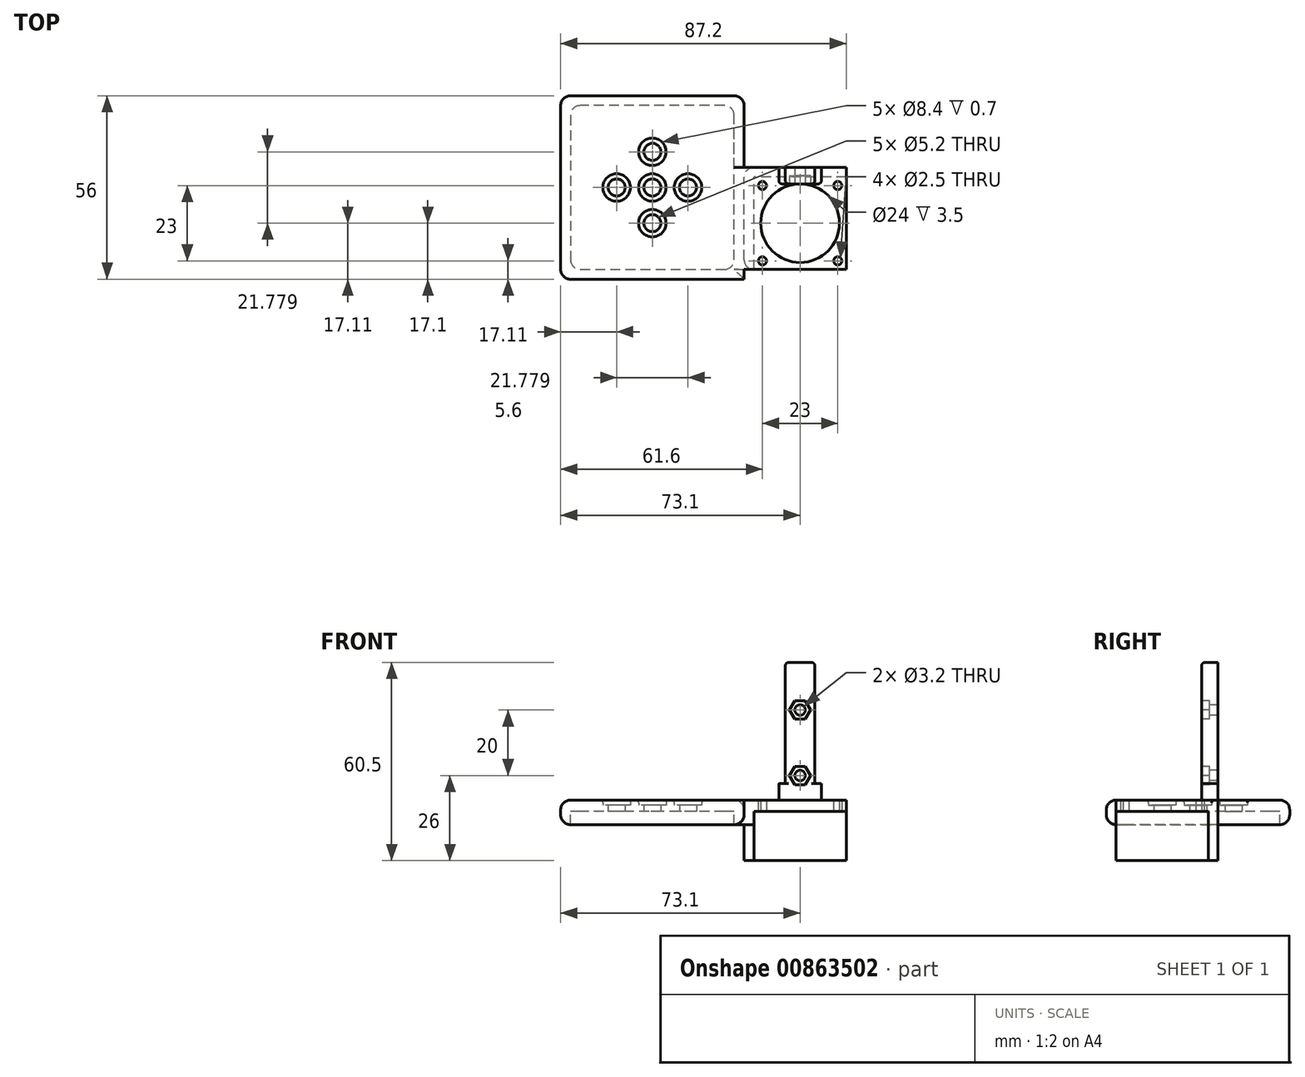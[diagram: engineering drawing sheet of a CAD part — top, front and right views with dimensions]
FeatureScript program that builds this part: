
annotation { "Feature Type Name" : "Feature", "Feature Type Description" : "" }
export const myFeature = defineFeature(function(context is Context, id is Id, definition is map)
    precondition{}
    {
        {
            var Q0;
            Q0=qCreatedBy(makeId("Top.planeOp"),FACE);
            var sketch = newSketch(context, id + "F0", { "sketchPlane" : qUnion([Q0])});
            skLineSegment(sketch, "E0.bottom", {"start": v(0, 0) * mm, "end": v(-28.2, 0) * mm});
            skLineSegment(sketch, "E0.top", {"start": v(0, 28.2) * mm, "end": v(-28.2, 28.2) * mm});
            skLineSegment(sketch, "E0.left", {"start": v(0, 0) * mm, "end": v(0, 28.2) * mm});
            skLineSegment(sketch, "E0.right", {"start": v(-28.2, 0) * mm, "end": v(-28.2, 28.2) * mm});
            skCircle(sketch, "E1", {"center": v(-14.1, 14.1) * mm, "radius": 12 * mm});
            skPoint(sketch, "E1.centerSnap0", {"position": v(0, 14.1) * mm});
            skPoint(sketch, "E1.centerSnap1", {"position": v(-14.1, 0) * mm});
            skCircle(sketch, "E2", {"center": v(-2.6, 25.6) * mm, "radius": 1.25 * mm});
            skCircle(sketch, "E3.0.1.0", {"center": v(-2.6, 2.6) * mm, "radius": 1.25 * mm});
            skCircle(sketch, "E3.1.0.0", {"center": v(-25.6, 25.6) * mm, "radius": 1.25 * mm});
            skCircle(sketch, "E3.1.1.0", {"center": v(-25.6, 2.6) * mm, "radius": 1.25 * mm});
            skLineSegment(sketch, "E3.direction1", {"start": v(-2.6, 25.6) * mm, "end": v(-25.6, 25.6) * mm, "construction": true});
            skLineSegment(sketch, "E3.direction2", {"start": v(-2.6, 25.6) * mm, "end": v(-2.6, 2.6) * mm, "construction": true});
            skPoint(sketch, "E4.startSnap0", {"position": v(-14.1, 25.6) * mm});
            skLineSegment(sketch, "E5", {"start": v(0, 31.1) * mm, "end": v(0, 28.2) * mm});
            skLineSegment(sketch, "E6", {"start": v(0, 31.1) * mm, "end": v(-28.2, 31.1) * mm});
            skLineSegment(sketch, "E7", {"start": v(-28.2, 31.1) * mm, "end": v(-28.2, 28.2) * mm});
            skLineSegment(sketch, "E8", {"start": v(-28.2, 0) * mm, "end": v(-31.2, 0) * mm});
            skLineSegment(sketch, "E9", {"start": v(-31.2, 0) * mm, "end": v(-31.2, -3) * mm, "construction": true});
            skLineSegment(sketch, "E10.bottom", {"start": v(-31.2, -3) * mm, "end": v(-87.2, -3) * mm});
            skLineSegment(sketch, "E10.top", {"start": v(-31.2, 53) * mm, "end": v(-87.2, 53) * mm});
            skLineSegment(sketch, "E10.left", {"start": v(-31.2, -3) * mm, "end": v(-31.2, 53) * mm});
            skLineSegment(sketch, "E10.right", {"start": v(-87.2, -3) * mm, "end": v(-87.2, 53) * mm});
            skLineSegment(sketch, "E11", {"start": v(-28.2, 31.1) * mm, "end": v(-31.2, 31.1) * mm});
            skLineSegment(sketch, "E12", {"start": v(-84.2, 50) * mm, "end": v(-84.2, 0) * mm});
            skLineSegment(sketch, "E13", {"start": v(-84.2, 0) * mm, "end": v(-34.2, 0) * mm});
            skLineSegment(sketch, "E14", {"start": v(-34.2, 0) * mm, "end": v(-34.2, 50) * mm});
            skLineSegment(sketch, "E15", {"start": v(-34.2, 50) * mm, "end": v(-84.2, 50) * mm});
            skPoint(sketch, "E16", {"position": v(-59.2, 25) * mm});
            skPoint(sketch, "E16.positionSnap0", {"position": v(-84.2, 25) * mm});
            skPoint(sketch, "E16.positionSnap1", {"position": v(-59.2, 50) * mm});
            skCircle(sketch, "E17", {"center": v(-59.2, 25) * mm, "radius": 2.6 * mm});
            skCircle(sketch, "E18", {"center": v(-59.2, 25) * mm, "radius": 4.2 * mm});
            skCircle(sketch, "E19", {"center": v(-59.2, 35.89) * mm, "radius": 2.6 * mm});
            skCircle(sketch, "E20", {"center": v(-59.2, 35.89) * mm, "radius": 4.2 * mm});
            skCircle(sketch, "E21.1.0", {"center": v(-70.09, 25) * mm, "radius": 2.6 * mm});
            skCircle(sketch, "E21.1.1", {"center": v(-70.09, 25) * mm, "radius": 4.2 * mm});
            skCircle(sketch, "E21.2.0", {"center": v(-59.2, 14.11) * mm, "radius": 2.6 * mm});
            skCircle(sketch, "E21.2.1", {"center": v(-59.2, 14.11) * mm, "radius": 4.2 * mm});
            skCircle(sketch, "E21.3.0", {"center": v(-48.31, 25) * mm, "radius": 2.6 * mm});
            skCircle(sketch, "E21.3.1", {"center": v(-48.31, 25) * mm, "radius": 4.2 * mm});
            skSolve(sketch);
        }
        {
            var Q0;
            {var subQ6=sQuery(id+"F0.wireOp",EDGE,"E0.bottom");Q0=makeQuery(id+"F0.imprint","IMPRINT",FACE,{"disambiguationData":[TD([[makeQuery(id+"F0.imprint","IMPRINT",EDGE,{"derivedFrom":subQ6}),-1.0]])]});}
            var Q1;
            {var subQ4=sQuery(id+"F0.wireOp",EDGE,"ijPHqbvI-z4L9-HcXl-GGPW-hylEVIwZFws3");Q1=makeQuery(id+"F0.imprint","IMPRINT",FACE,{"disambiguationData":[TD([[makeQuery(id+"F0.imprint","IMPRINT",EDGE,{"derivedFrom":subQ4}),-1.0]])]});}
            var Q2;
            {var subQ5=sQuery(id+"F0.wireOp",EDGE,"m2Cxr2Ga-0o2j-HVXw-7p58-Pcn7Cvv0tEOK");Q2=makeQuery(id+"F0.imprint","IMPRINT",FACE,{"disambiguationData":[TD([[makeQuery(id+"F0.imprint","IMPRINT",EDGE,{"derivedFrom":subQ5}),1.0]])]});}
            var Q3;
            Q3=makeQuery(id+"F0.imprint","IMPRINT",FACE,{"disambiguationData":[TD([[makeQuery(id+"F0.imprint","IMPRINT",EDGE,{"derivedFrom":sQuery(id+"F0.wireOp",EDGE,"8loH9SmV-sh9J-LUzo-QlBY-makiSQwsu6jr")}),-1.0]])]});
            var Q4;
            {var subQ0=sQuery(id+"F0.wireOp",EDGE,"9hWyS0dG-HEyQ-yypX-yeBZ-Q9COCQ3kwopz.top");Q4=makeQuery(id+"F0.imprint","IMPRINT",FACE,{"disambiguationData":[TD([[makeQuery(id+"F0.imprint","IMPRINT",EDGE,{"derivedFrom":subQ0}),-1.0]])]});}
            var Q5;
            {var subQ3=sQuery(id+"F0.wireOp",EDGE,"NLWkRKNC-S5Q5-cDU1-KmpY-qmc1vbDf303U");Q5=makeQuery(id+"F0.imprint","IMPRINT",FACE,{"disambiguationData":[TD([[makeQuery(id+"F0.imprint","IMPRINT",EDGE,{"derivedFrom":subQ3}),1.0]])]});}
            var Q6;
            {var subQ0=sQuery(id+"F0.wireOp",EDGE,"9hWyS0dG-HEyQ-yypX-yeBZ-Q9COCQ3kwopz.bottom");Q6=makeQuery(id+"F0.imprint","IMPRINT",FACE,{"disambiguationData":[TD([[makeQuery(id+"F0.imprint","IMPRINT",EDGE,{"derivedFrom":subQ0}),1.0]])]});}
            var Q7;
            {var subQ6=sQuery(id+"F0.wireOp",EDGE,"E4");Q7=makeQuery(id+"F0.imprint","IMPRINT",FACE,{"disambiguationData":[TD([[makeQuery(id+"F0.imprint","IMPRINT",EDGE,{"derivedFrom":subQ6}),-1.0]])]});}
            var Q8;
            {var subQ5=sQuery(id+"F0.wireOp",EDGE,"mFEbcyhE-I2m0-IbpG-fMGd-iVe9TuxLjYg8");Q8=makeQuery(id+"F0.imprint","IMPRINT",FACE,{"disambiguationData":[TD([[makeQuery(id+"F0.imprint","IMPRINT",EDGE,{"derivedFrom":subQ5}),-1.0]])]});}
            var Q9;
            {var subQ0=sQuery(id+"F0.wireOp",EDGE,"E0.top");Q9=makeQuery(id+"F0.imprint","IMPRINT",FACE,{"disambiguationData":[TD([[makeQuery(id+"F0.imprint","IMPRINT",EDGE,{"derivedFrom":subQ0}),-1.0]])]});}
            var Q10;
            {var subQ5=sQuery(id+"F0.wireOp",EDGE,"lu1baBKB-0tmX-wPb9-EPOR-MeIyYVtMshRU");Q10=makeQuery(id+"F0.imprint","IMPRINT",FACE,{"disambiguationData":[TD([[makeQuery(id+"F0.imprint","IMPRINT",EDGE,{"derivedFrom":subQ5}),-1.0]])]});}
            var Q11;
            {var subQ1=sQuery(id+"F0.wireOp",EDGE,"7PjgIpir-cJoU-ZLOv-uaDD-36FM32oQSfDl.top");Q11=makeQuery(id+"F0.imprint","IMPRINT",FACE,{"disambiguationData":[TD([[makeQuery(id+"F0.imprint","IMPRINT",EDGE,{"derivedFrom":subQ1}),1.0]])]});}
            var Q12;
            {var subQ3=sQuery(id+"F0.wireOp",EDGE,"xbB81sAq-Xaiy-Ms8t-QkRO-Xj2NnZmD8rnq");Q12=makeQuery(id+"F0.imprint","IMPRINT",FACE,{"disambiguationData":[TD([[makeQuery(id+"F0.imprint","IMPRINT",EDGE,{"derivedFrom":subQ3}),-1.0]])]});}
            var Q13;
            Q13=makeQuery(id+"F0.imprint","IMPRINT",FACE,{"disambiguationData":[TD([[makeQuery(id+"F0.imprint","IMPRINT",EDGE,{"derivedFrom":sQuery(id+"F0.wireOp",EDGE,"E0.right")}),1.0]])]});
            var Q14;
            {var subQ0=sQuery(id+"F0.wireOp",EDGE,"XYQOdFon-8ze7-kMVV-HPu9-pt2qhsvfgXNz");Q14=makeQuery(id+"F0.imprint","IMPRINT",FACE,{"disambiguationData":[TD([[makeQuery(id+"F0.imprint","IMPRINT",EDGE,{"derivedFrom":subQ0}),1.0]])]});}
            var Q15;
            {var subQ3=sQuery(id+"F0.wireOp",EDGE,"bGz3AujC-m2g5-EDBu-aNqw-dt0JoBSHWJhe");Q15=makeQuery(id+"F0.imprint","IMPRINT",FACE,{"disambiguationData":[TD([[makeQuery(id+"F0.imprint","IMPRINT",EDGE,{"derivedFrom":subQ3}),-1.0]])]});}
            var Q16;
            {var subQ0=sQuery(id+"F0.wireOp",EDGE,"qGMF6F5y-CSdx-2Ybo-XQKX-Ya8MyXLlpcJf");Q16=makeQuery(id+"F0.imprint","IMPRINT",FACE,{"disambiguationData":[TD([[makeQuery(id+"F0.imprint","IMPRINT",EDGE,{"derivedFrom":subQ0}),-1.0]])]});}
            var Q17;
            {var subQ4=sQuery(id+"F0.wireOp",EDGE,"E10.bottom");Q17=makeQuery(id+"F0.imprint","IMPRINT",FACE,{"disambiguationData":[TD([[makeQuery(id+"F0.imprint","IMPRINT",EDGE,{"derivedFrom":subQ4}),-1.0]])]});}
            var Q18;
            {var subQ0=sQuery(id+"F0.wireOp",EDGE,"PibB2iq3-5r3C-sdaA-aypm-pyxTfNWSrPnX");Q18=makeQuery(id+"F0.imprint","IMPRINT",FACE,{"disambiguationData":[TD([[makeQuery(id+"F0.imprint","IMPRINT",EDGE,{"derivedFrom":subQ0}),1.0]])]});}
            var Q19;
            Q19=makeQuery(id+"F0.imprint","IMPRINT",FACE,{"disambiguationData":[TD([[makeQuery(id+"F0.imprint","IMPRINT",EDGE,{"derivedFrom":sQuery(id+"F0.wireOp",EDGE,"E12")}),1.0]])]});
            extrude(context, id + "F1", {"entities" : qUnion([Q0, Q1, Q2, Q3, Q4, Q5, Q6, Q7, Q8, Q9, Q10, Q11, Q12, Q13, Q14, Q15, Q16, Q17, Q18, Q19]), "depth" : 3.5 * mm, "offsetDistance" : 25 * mm});
        }
        {
            var Q0;
            {var subQ4=sQuery(id+"F0.wireOp",EDGE,"E10.bottom");Q0=makeQuery(id+"F0.imprint","IMPRINT",FACE,{"disambiguationData":[TD([[makeQuery(id+"F0.imprint","IMPRINT",EDGE,{"derivedFrom":subQ4}),-1.0]])]});}
            extrude(context, id + "F2", {"entities" : qUnion([Q0]), "operationType" : NewBodyOperationType.ADD, "oppositeDirection" : true, "depth" : 4 * mm, "offsetDistance" : 25 * mm});
        }
        {
            var Q0;
            Q0=makeQuery(id+"F0.imprint","IMPRINT",FACE,{"disambiguationData":[TD([[makeQuery(id+"F0.imprint","IMPRINT",EDGE,{"derivedFrom":sQuery(id+"F0.wireOp",EDGE,"E19")}),-1.0]])]});
            var Q1;
            Q1=makeQuery(id+"F0.imprint","IMPRINT",FACE,{"disambiguationData":[TD([[makeQuery(id+"F0.imprint","IMPRINT",EDGE,{"derivedFrom":sQuery(id+"F0.wireOp",EDGE,"E21.3.0")}),-1.0]])]});
            var Q2;
            Q2=makeQuery(id+"F0.imprint","IMPRINT",FACE,{"disambiguationData":[TD([[makeQuery(id+"F0.imprint","IMPRINT",EDGE,{"derivedFrom":sQuery(id+"F0.wireOp",EDGE,"E17")}),-1.0]])]});
            var Q3;
            Q3=makeQuery(id+"F0.imprint","IMPRINT",FACE,{"disambiguationData":[TD([[makeQuery(id+"F0.imprint","IMPRINT",EDGE,{"derivedFrom":sQuery(id+"F0.wireOp",EDGE,"E21.1.0")}),-1.0]])]});
            var Q4;
            Q4=makeQuery(id+"F0.imprint","IMPRINT",FACE,{"disambiguationData":[TD([[makeQuery(id+"F0.imprint","IMPRINT",EDGE,{"derivedFrom":sQuery(id+"F0.wireOp",EDGE,"E21.2.0")}),-1.0]])]});
            extrude(context, id + "F3", {"entities" : qUnion([Q0, Q1, Q2, Q3, Q4]), "operationType" : NewBodyOperationType.ADD, "depth" : 2 * mm, "offsetDistance" : 25 * mm});
        }
        {
            var Q0;
            Q0=makeQuery(id+"F1.opExtrude","CAP_FACE",FACE,{"disambiguationData":[OSD([sQuery(id+"F0.wireOp",EDGE,"E0.bottom"),sQuery(id+"F0.wireOp",EDGE,"E0.left"),sQuery(id+"F0.wireOp",EDGE,"E1"),sQuery(id+"F0.wireOp",EDGE,"E2"),sQuery(id+"F0.wireOp",EDGE,"E3.0.1.0"),sQuery(id+"F0.wireOp",EDGE,"E3.1.0.0"),sQuery(id+"F0.wireOp",EDGE,"E3.1.1.0"),sQuery(id+"F0.wireOp",EDGE,"9hWyS0dG-HEyQ-yypX-yeBZ-Q9COCQ3kwopz.bottom"),sQuery(id+"F0.wireOp",EDGE,"9hWyS0dG-HEyQ-yypX-yeBZ-Q9COCQ3kwopz.top"),sQuery(id+"F0.wireOp",EDGE,"9hWyS0dG-HEyQ-yypX-yeBZ-Q9COCQ3kwopz.left"),sQuery(id+"F0.wireOp",EDGE,"8loH9SmV-sh9J-LUzo-QlBY-makiSQwsu6jr"),sQuery(id+"F0.wireOp",EDGE,"cz2AWorx-eusL-XrBm-fWZu-7YGwTg6LLj23"),sQuery(id+"F0.wireOp",EDGE,"029e4b47-2b3b-455f-a0ee-34a0f4a43a5b.1.1"),sQuery(id+"F0.wireOp",EDGE,"029e4b47-2b3b-455f-a0ee-34a0f4a43a5b.2.1"),sQuery(id+"F0.wireOp",EDGE,"029e4b47-2b3b-455f-a0ee-34a0f4a43a5b.3.1"),sQuery(id+"F0.wireOp",EDGE,"NLWkRKNC-S5Q5-cDU1-KmpY-qmc1vbDf303U"),sQuery(id+"F0.wireOp",EDGE,"zs0ojhJG-X6Sq-BrWQ-kWkG-rbSZWmPVnEDv"),sQuery(id+"F0.wireOp",EDGE,"vGF2y9MP-X188-q6Oo-Al50-q7mYZCjIZBZr"),sQuery(id+"F0.wireOp",EDGE,"E5"),sQuery(id+"F0.wireOp",EDGE,"E6")])],"isStart":false});
            var sketch = newSketch(context, id + "F4", { "sketchPlane" : qUnion([Q0])});
            skLineSegment(sketch, "E22", {"start": v(-14.1, 26.1) * mm, "end": v(-18.6, 26.1) * mm});
            skLineSegment(sketch, "E23", {"start": v(-18.6, 26.1) * mm, "end": v(-18.6, 31.1) * mm});
            skLineSegment(sketch, "E24", {"start": v(-18.6, 31.1) * mm, "end": v(-9.6, 31.1) * mm});
            skLineSegment(sketch, "E25", {"start": v(-9.6, 31.1) * mm, "end": v(-9.6, 26.1) * mm});
            skLineSegment(sketch, "E26", {"start": v(-9.6, 26.1) * mm, "end": v(-14.1, 26.1) * mm});
            skLineSegment(sketch, "E27", {"start": v(-18.6, 26.1) * mm, "end": v(-20.6, 26.1) * mm});
            skLineSegment(sketch, "E28", {"start": v(-20.6, 26.1) * mm, "end": v(-20.6, 31.1) * mm});
            skLineSegment(sketch, "E29", {"start": v(-20.6, 31.1) * mm, "end": v(-18.6, 31.1) * mm});
            skLineSegment(sketch, "E30", {"start": v(-9.6, 26.1) * mm, "end": v(-7.6, 26.1) * mm});
            skLineSegment(sketch, "E31", {"start": v(-7.6, 26.1) * mm, "end": v(-7.6, 31.1) * mm});
            skLineSegment(sketch, "E32", {"start": v(-7.6, 31.1) * mm, "end": v(-9.6, 31.1) * mm});
            skSolve(sketch);
        }
        {
            var Q0;
            Q0=makeQuery(id+"F4.imprint","IMPRINT",FACE,{"disambiguationData":[TD([[makeQuery(id+"F4.imprint","IMPRINT",EDGE,{"derivedFrom":sQuery(id+"F4.wireOp",EDGE,"E22")}),-1.0]])]});
            extrude(context, id + "F5", {"entities" : qUnion([Q0]), "operationType" : NewBodyOperationType.ADD, "depth" : 42 * mm, "offsetDistance" : 25 * mm});
        }
        {
            var Q0;
            Q0=makeQuery(id+"F4.imprint","IMPRINT",FACE,{"disambiguationData":[TD([[makeQuery(id+"F4.imprint","IMPRINT",EDGE,{"derivedFrom":sQuery(id+"F4.wireOp",EDGE,"E23")}),1.0]])]});
            var Q1;
            Q1=makeQuery(id+"F4.imprint","IMPRINT",FACE,{"disambiguationData":[TD([[makeQuery(id+"F4.imprint","IMPRINT",EDGE,{"derivedFrom":sQuery(id+"F4.wireOp",EDGE,"E25")}),1.0]])]});
            extrude(context, id + "F6", {"entities" : qUnion([Q0, Q1]), "operationType" : NewBodyOperationType.ADD, "depth" : 5 * mm, "offsetDistance" : 25 * mm});
        }
        {
            var Q0;
            Q0=makeQuery(id+"F5.opExtrude","SWEPT_FACE",FACE,{"disambiguationData":[OSD([sQuery(id+"F4.wireOp",EDGE,"E22"),sQuery(id+"F4.wireOp",EDGE,"E26")])]});
            var sketch = newSketch(context, id + "F7", { "sketchPlane" : qUnion([Q0])});
            skLineSegment(sketch, "E33", {"start": v(-14.1, 45.5) * mm, "end": v(-14.1, 3.5) * mm, "construction": true});
            skCircle(sketch, "E34", {"center": v(-14.1, 11) * mm, "radius": 1.6 * mm});
            skCircle(sketch, "E35", {"center": v(-14.1, 31) * mm, "radius": 1.6 * mm});
            skCircle(sketch, "E36.cCircle", {"center": v(-14.1, 11) * mm, "radius": 2.8 * mm, "construction": true});
            skLineSegment(sketch, "E36.0", {"start": v(-15.72, 13.8) * mm, "end": v(-12.48, 13.8) * mm});
            skLineSegment(sketch, "E36.1", {"start": v(-12.48, 13.8) * mm, "end": v(-10.87, 11) * mm});
            skLineSegment(sketch, "E36.2", {"start": v(-10.87, 11) * mm, "end": v(-12.48, 8.2) * mm});
            skLineSegment(sketch, "E36.3", {"start": v(-12.48, 8.2) * mm, "end": v(-15.72, 8.2) * mm});
            skLineSegment(sketch, "E36.4", {"start": v(-15.72, 8.2) * mm, "end": v(-17.33, 11) * mm});
            skLineSegment(sketch, "E36.5", {"start": v(-17.33, 11) * mm, "end": v(-15.72, 13.8) * mm});
            skPoint(sketch, "E36.0.midPoint", {"position": v(-14.1, 13.8) * mm});
            skCircle(sketch, "E37.cCircle", {"center": v(-14.1, 31) * mm, "radius": 2.8 * mm, "construction": true});
            skLineSegment(sketch, "E37.0", {"start": v(-15.72, 33.8) * mm, "end": v(-12.48, 33.8) * mm});
            skLineSegment(sketch, "E37.1", {"start": v(-12.48, 33.8) * mm, "end": v(-10.87, 31) * mm});
            skLineSegment(sketch, "E37.2", {"start": v(-10.87, 31) * mm, "end": v(-12.48, 28.2) * mm});
            skLineSegment(sketch, "E37.3", {"start": v(-12.48, 28.2) * mm, "end": v(-15.72, 28.2) * mm});
            skLineSegment(sketch, "E37.4", {"start": v(-15.72, 28.2) * mm, "end": v(-17.33, 31) * mm});
            skLineSegment(sketch, "E37.5", {"start": v(-17.33, 31) * mm, "end": v(-15.72, 33.8) * mm});
            skPoint(sketch, "E37.0.midPoint", {"position": v(-14.1, 33.8) * mm});
            skSolve(sketch);
        }
        {
            var Q0;
            Q0=makeQuery(id+"F7.imprint","IMPRINT",FACE,{"disambiguationData":[TD([[makeQuery(id+"F7.imprint","IMPRINT",EDGE,{"derivedFrom":sQuery(id+"F7.wireOp",EDGE,"E35")}),1.0]])]});
            var Q1;
            Q1=makeQuery(id+"F7.imprint","IMPRINT",FACE,{"disambiguationData":[TD([[makeQuery(id+"F7.imprint","IMPRINT",EDGE,{"derivedFrom":sQuery(id+"F7.wireOp",EDGE,"E34")}),1.0]])]});
            extrude(context, id + "F8", {"entities" : qUnion([Q0, Q1]), "operationType" : NewBodyOperationType.REMOVE, "oppositeDirection" : true, "depth" : 6 * mm, "offsetDistance" : 25 * mm});
        }
        {
            var Q0;
            Q0=makeQuery(id+"F7.imprint","IMPRINT",FACE,{"disambiguationData":[TD([[makeQuery(id+"F7.imprint","IMPRINT",EDGE,{"derivedFrom":sQuery(id+"F7.wireOp",EDGE,"E35")}),-1.0]])]});
            var Q1;
            Q1=makeQuery(id+"F7.imprint","IMPRINT",FACE,{"disambiguationData":[TD([[makeQuery(id+"F7.imprint","IMPRINT",EDGE,{"derivedFrom":sQuery(id+"F7.wireOp",EDGE,"E34")}),-1.0]])]});
            extrude(context, id + "F9", {"entities" : qUnion([Q0, Q1]), "operationType" : NewBodyOperationType.REMOVE, "oppositeDirection" : true, "depth" : 2.5 * mm, "offsetDistance" : 25 * mm});
        }
        {
            var Q0;
            Q0=makeQuery(id+"F0.imprint","IMPRINT",FACE,{"disambiguationData":[TD([[makeQuery(id+"F0.imprint","IMPRINT",EDGE,{"derivedFrom":sQuery(id+"F0.wireOp",EDGE,"E0.right")}),1.0]])]});
            extrude(context, id + "F10", {"entities" : qUnion([Q0]), "operationType" : NewBodyOperationType.ADD, "oppositeDirection" : true, "depth" : 15 * mm, "offsetDistance" : 25 * mm});
        }
        {
            var Q0;
            Q0=makeQuery(id+"F5.opExtrude","SWEPT_EDGE",EDGE,{"disambiguationData":[OSD([sQuery(id+"F4.wireOp",EDGE,"E22"),sQuery(id+"F4.wireOp",EDGE,"E23")])]});
            var Q1;
            Q1=makeQuery(id+"F5.opExtrude","SWEPT_EDGE",EDGE,{"disambiguationData":[OSD([sQuery(id+"F4.wireOp",EDGE,"E25"),sQuery(id+"F4.wireOp",EDGE,"E26")])]});
            var Q2;
            Q2=makeQuery(id+"F5.opExtrude","CAP_EDGE",EDGE,{"disambiguationData":[OSD([sQuery(id+"F4.wireOp",EDGE,"E22"),sQuery(id+"F4.wireOp",EDGE,"E26")])],"isStart":false});
            var Q3;
            Q3=makeQuery(id+"F5.opExtrude","CAP_EDGE",EDGE,{"disambiguationData":[OSD([sQuery(id+"F4.wireOp",EDGE,"E25")])],"isStart":false});
            var Q4;
            Q4=makeQuery(id+"F5.opExtrude","CAP_EDGE",EDGE,{"disambiguationData":[OSD([sQuery(id+"F4.wireOp",EDGE,"E23")])],"isStart":false});
            var Q5;
            Q5=makeQuery(id+"F6.opExtrude","SWEPT_EDGE",EDGE,{"disambiguationData":[OSD([sQuery(id+"F4.wireOp",EDGE,"E27"),sQuery(id+"F4.wireOp",EDGE,"E28")])]});
            var Q6;
            Q6=makeQuery(id+"F6.opExtrude","SWEPT_EDGE",EDGE,{"disambiguationData":[OSD([sQuery(id+"F4.wireOp",EDGE,"E30"),sQuery(id+"F4.wireOp",EDGE,"E31")])]});
            var Q7;
            Q7=makeQuery(id+"F6.opExtrude","CAP_EDGE",EDGE,{"disambiguationData":[OSD([sQuery(id+"F4.wireOp",EDGE,"E31")])],"isStart":true});
            fillet(context, id + "F11", {"entities" : qUnion([Q0, Q1, Q2, Q3, Q4, Q5, Q6, Q7]), "tangentPropagation" : true, "radius" : 1 * mm, "defaultsChanged" : false, "vertexSettings" : [], "allowEdgeOverflow" : false});
        }
        {
            var Q0;
            Q0=makeQuery(id+"F1.opExtrude","CAP_EDGE",EDGE,{"disambiguationData":[OSD([sQuery(id+"F0.wireOp",EDGE,"E20")])],"isStart":false});
            var Q1;
            Q1=makeQuery(id+"F1.opExtrude","CAP_EDGE",EDGE,{"disambiguationData":[OSD([sQuery(id+"F0.wireOp",EDGE,"E21.3.1")])],"isStart":false});
            var Q2;
            Q2=makeQuery(id+"F1.opExtrude","CAP_EDGE",EDGE,{"disambiguationData":[OSD([sQuery(id+"F0.wireOp",EDGE,"E18")])],"isStart":false});
            var Q3;
            Q3=makeQuery(id+"F1.opExtrude","CAP_EDGE",EDGE,{"disambiguationData":[OSD([sQuery(id+"F0.wireOp",EDGE,"E21.1.1")])],"isStart":false});
            var Q4;
            Q4=makeQuery(id+"F1.opExtrude","CAP_EDGE",EDGE,{"disambiguationData":[OSD([sQuery(id+"F0.wireOp",EDGE,"E21.2.1")])],"isStart":false});
            fillet(context, id + "F12", {"entities" : qUnion([Q0, Q1, Q2, Q3, Q4]), "tangentPropagation" : true, "radius" : 0.8 * mm, "defaultsChanged" : false, "vertexSettings" : [], "allowEdgeOverflow" : false});
        }
        {
            var Q0;
            {var subQ0=sQuery(id+"F0.wireOp",EDGE,"E10.right");var subQ1=sQuery(id+"F0.wireOp",EDGE,"E10.bottom");Q0=makeQuery(id+"F2.boolean.opBoolean","MERGE",EDGE,{"derivedFrom":[makeQuery(id+"F1.opExtrude","SWEPT_EDGE",EDGE,{"disambiguationData":[OSD([subQ1,subQ0])]}),makeQuery(id+"F2.opExtrude","SWEPT_EDGE",EDGE,{"disambiguationData":[OSD([subQ1,subQ0])]})]});}
            var Q1;
            Q1=makeQuery(id+"F2.opExtrude","SWEPT_EDGE",EDGE,{"disambiguationData":[OSD([sQuery(id+"F0.wireOp",EDGE,"E12"),sQuery(id+"F0.wireOp",EDGE,"E13")])]});
            var Q2;
            Q2=makeQuery(id+"F2.opExtrude","SWEPT_EDGE",EDGE,{"disambiguationData":[OSD([sQuery(id+"F0.wireOp",EDGE,"E13"),sQuery(id+"F0.wireOp",EDGE,"E14")])]});
            var Q3;
            Q3=makeQuery(id+"F2.opExtrude","SWEPT_EDGE",EDGE,{"disambiguationData":[OSD([sQuery(id+"F0.wireOp",EDGE,"E14"),sQuery(id+"F0.wireOp",EDGE,"E15")])]});
            var Q4;
            Q4=makeQuery(id+"F2.opExtrude","SWEPT_EDGE",EDGE,{"disambiguationData":[OSD([sQuery(id+"F0.wireOp",EDGE,"E12"),sQuery(id+"F0.wireOp",EDGE,"E15")])]});
            var Q5;
            {var subQ0=sQuery(id+"F0.wireOp",EDGE,"E10.right");var subQ1=sQuery(id+"F0.wireOp",EDGE,"E10.top");Q5=makeQuery(id+"F2.boolean.opBoolean","MERGE",EDGE,{"derivedFrom":[makeQuery(id+"F1.opExtrude","SWEPT_EDGE",EDGE,{"disambiguationData":[OSD([subQ1,subQ0])]}),makeQuery(id+"F2.opExtrude","SWEPT_EDGE",EDGE,{"disambiguationData":[OSD([subQ1,subQ0])]})]});}
            var Q6;
            {var subQ0=sQuery(id+"F0.wireOp",EDGE,"E10.left");var subQ1=sQuery(id+"F0.wireOp",EDGE,"E10.top");Q6=makeQuery(id+"F2.boolean.opBoolean","MERGE",EDGE,{"derivedFrom":[makeQuery(id+"F1.opExtrude","SWEPT_EDGE",EDGE,{"disambiguationData":[OSD([subQ1,subQ0])]}),makeQuery(id+"F2.opExtrude","SWEPT_EDGE",EDGE,{"disambiguationData":[OSD([subQ1,subQ0])]})]});}
            var Q7;
            Q7=makeQuery(id+"F1.opExtrude","CAP_EDGE",EDGE,{"disambiguationData":[OSD([sQuery(id+"F0.wireOp",EDGE,"E10.right")])],"isStart":false});
            var Q8;
            Q8=makeQuery(id+"F1.opExtrude","CAP_EDGE",EDGE,{"disambiguationData":[OSD([sQuery(id+"F0.wireOp",EDGE,"E10.top")])],"isStart":false});
            var Q9;
            {var subQ0=sQuery(id+"F0.wireOp",EDGE,"E10.left");Q9=makeQuery(id+"F1.opExtrude","CAP_EDGE",EDGE,{"disambiguationData":[OSD([subQ0]),TDD([makeQuery(id+"F0.imprint","IMPRINT",EDGE,{"disambiguationData":[TD([[makeQuery(id+"F0.imprint","INTERSECT",VERTEX,{"derivedFrom":[sQuery(id+"F0.wireOp",EDGE,"E10.top"),subQ0]}),1.0]])],"derivedFrom":subQ0})])],"isStart":false});}
            var Q10;
            Q10=makeQuery(id+"F1.opExtrude","CAP_EDGE",EDGE,{"disambiguationData":[OSD([sQuery(id+"F0.wireOp",EDGE,"E10.bottom")])],"isStart":false});
            fillet(context, id + "F13", {"entities" : qUnion([Q0, Q1, Q2, Q3, Q4, Q5, Q6, Q7, Q8, Q9, Q10]), "tangentPropagation" : true, "radius" : 3 * mm, "defaultsChanged" : true, "vertexSettings" : [], "allowEdgeOverflow" : false});
        }
        {
            var Q0;
            {var subQ0=sQuery(id+"F0.wireOp",EDGE,"E10.left");Q0=makeQuery(id+"F10.boolean.opBoolean","SPLIT",EDGE,{"disambiguationData":[topologyDisambiguationEdgeConnected([makeQuery(id+"F2.opExtrude","CAP_FACE",FACE,{"disambiguationData":[OSD([sQuery(id+"F0.wireOp",EDGE,"E10.bottom"),sQuery(id+"F0.wireOp",EDGE,"E10.top"),subQ0,sQuery(id+"F0.wireOp",EDGE,"E10.right"),sQuery(id+"F0.wireOp",EDGE,"E12"),sQuery(id+"F0.wireOp",EDGE,"E13"),sQuery(id+"F0.wireOp",EDGE,"E14"),sQuery(id+"F0.wireOp",EDGE,"E15")])],"isStart":false}),makeQuery(id+"F10.opExtrude","SWEPT_FACE",FACE,{"disambiguationData":[OSD([subQ0])]})])],"derivedFrom":makeQuery(id+"F2.opExtrude","CAP_EDGE",EDGE,{"disambiguationData":[OSD([subQ0])],"isStart":false})});}
            fillet(context, id + "F14", {"entities" : qUnion([Q0]), "tangentPropagation" : true, "radius" : 3 * mm, "defaultsChanged" : false, "vertexSettings" : [], "allowEdgeOverflow" : false});
        }
        {
            var Q0;
            {var subQ0=sQuery(id+"F0.wireOp",EDGE,"E11");var subQ1=sQuery(id+"F0.wireOp",EDGE,"E10.left");var subQ2=sQuery(id+"F0.wireOp",EDGE,"E10.bottom");var subQ3=sQuery(id+"F0.wireOp",EDGE,"E10.top");Q0=makeQuery(id+"F14.opFillet","TWEAK_EDGE",EDGE,{"derivedFrom":[makeQuery(id+"F10.boolean.opBoolean","TWEAK_VERTEX",VERTEX,{"derivedFrom":[makeQuery(id+"F2.opExtrude","CAP_FACE",FACE,{"disambiguationData":[OSD([subQ2,subQ3,subQ1,sQuery(id+"F0.wireOp",EDGE,"E10.right"),sQuery(id+"F0.wireOp",EDGE,"E12"),sQuery(id+"F0.wireOp",EDGE,"E13"),sQuery(id+"F0.wireOp",EDGE,"E14"),sQuery(id+"F0.wireOp",EDGE,"E15")])],"isStart":false}),makeQuery(id+"F2.boolean.opBoolean","MERGE",FACE,{"derivedFrom":[makeQuery(id+"F1.opExtrude","SWEPT_FACE",FACE,{"disambiguationData":[OSD([subQ1]),TDD([makeQuery(id+"F0.imprint","IMPRINT",EDGE,{"disambiguationData":[TD([[makeQuery(id+"F0.imprint","INTERSECT",VERTEX,{"derivedFrom":[subQ3,subQ1]}),1.0]])],"derivedFrom":subQ1})])]}),makeQuery(id+"F1.opExtrude","SWEPT_FACE",FACE,{"disambiguationData":[OSD([subQ1]),TDD([makeQuery(id+"F0.imprint","IMPRINT",EDGE,{"disambiguationData":[TD([[makeQuery(id+"F0.imprint","INTERSECT",VERTEX,{"derivedFrom":[sQuery(id+"F0.wireOp",EDGE,"E8"),subQ1]}),1.0]])],"derivedFrom":subQ1})])]}),makeQuery(id+"F2.opExtrude","SWEPT_FACE",FACE,{"disambiguationData":[OSD([subQ1])]})]}),makeQuery(id+"F5.boolean.opBoolean","MERGE",FACE,{"derivedFrom":[makeQuery(id+"F1.opExtrude","SWEPT_FACE",FACE,{"disambiguationData":[OSD([sQuery(id+"F0.wireOp",EDGE,"E6"),subQ0])]}),makeQuery(id+"F5.opExtrude","SWEPT_FACE",FACE,{"disambiguationData":[OSD([sQuery(id+"F4.wireOp",EDGE,"E24")])]})]}),makeQuery(id+"F10.opExtrude","SWEPT_FACE",FACE,{"disambiguationData":[OSD([subQ1])]}),makeQuery(id+"F10.opExtrude","SWEPT_FACE",FACE,{"disambiguationData":[OSD([subQ0])]})]})]});}
            var Q1;
            {var subQ0=sQuery(id+"F0.wireOp",EDGE,"E11");var subQ1=sQuery(id+"F0.wireOp",EDGE,"E10.left");Q1=makeQuery(id+"F10.boolean.opBoolean","MERGE",EDGE,{"derivedFrom":[makeQuery(id+"F1.opExtrude","SWEPT_EDGE",EDGE,{"disambiguationData":[OSD([subQ1,subQ0])]}),makeQuery(id+"F10.opExtrude","SWEPT_EDGE",EDGE,{"disambiguationData":[OSD([subQ1,subQ0])]})]});}
            var Q2;
            {var subQ0=sQuery(id+"F0.wireOp",EDGE,"E10.left");var subQ1=sQuery(id+"F0.wireOp",EDGE,"E8");Q2=makeQuery(id+"F10.boolean.opBoolean","MERGE",EDGE,{"derivedFrom":[makeQuery(id+"F1.opExtrude","SWEPT_EDGE",EDGE,{"disambiguationData":[OSD([subQ1,subQ0])]}),makeQuery(id+"F10.opExtrude","SWEPT_EDGE",EDGE,{"disambiguationData":[OSD([subQ1,subQ0])]})]});}
            var Q3;
            {var subQ0=sQuery(id+"F0.wireOp",EDGE,"E10.left");var subQ1=sQuery(id+"F0.wireOp",EDGE,"E8");var subQ2=sQuery(id+"F0.wireOp",EDGE,"E10.bottom");var subQ3=sQuery(id+"F0.wireOp",EDGE,"E10.top");Q3=makeQuery(id+"F14.opFillet","TWEAK_EDGE",EDGE,{"derivedFrom":[makeQuery(id+"F10.boolean.opBoolean","TWEAK_VERTEX",VERTEX,{"derivedFrom":[makeQuery(id+"F1.opExtrude","SWEPT_FACE",FACE,{"disambiguationData":[OSD([sQuery(id+"F0.wireOp",EDGE,"E0.bottom"),subQ1])]}),makeQuery(id+"F2.opExtrude","CAP_FACE",FACE,{"disambiguationData":[OSD([subQ2,subQ3,subQ0,sQuery(id+"F0.wireOp",EDGE,"E10.right"),sQuery(id+"F0.wireOp",EDGE,"E12"),sQuery(id+"F0.wireOp",EDGE,"E13"),sQuery(id+"F0.wireOp",EDGE,"E14"),sQuery(id+"F0.wireOp",EDGE,"E15")])],"isStart":false}),makeQuery(id+"F2.boolean.opBoolean","MERGE",FACE,{"derivedFrom":[makeQuery(id+"F1.opExtrude","SWEPT_FACE",FACE,{"disambiguationData":[OSD([subQ0]),TDD([makeQuery(id+"F0.imprint","IMPRINT",EDGE,{"disambiguationData":[TD([[makeQuery(id+"F0.imprint","INTERSECT",VERTEX,{"derivedFrom":[subQ3,subQ0]}),1.0]])],"derivedFrom":subQ0})])]}),makeQuery(id+"F1.opExtrude","SWEPT_FACE",FACE,{"disambiguationData":[OSD([subQ0]),TDD([makeQuery(id+"F0.imprint","IMPRINT",EDGE,{"disambiguationData":[TD([[makeQuery(id+"F0.imprint","INTERSECT",VERTEX,{"derivedFrom":[subQ1,subQ0]}),1.0]])],"derivedFrom":subQ0})])]}),makeQuery(id+"F2.opExtrude","SWEPT_FACE",FACE,{"disambiguationData":[OSD([subQ0])]})]}),makeQuery(id+"F10.opExtrude","SWEPT_FACE",FACE,{"disambiguationData":[OSD([subQ1])]}),makeQuery(id+"F10.opExtrude","SWEPT_FACE",FACE,{"disambiguationData":[OSD([subQ0])]})]})]});}
            fillet(context, id + "F15", {"entities" : qUnion([Q0, Q1, Q2, Q3]), "tangentPropagation" : true, "radius" : 3 * mm, "defaultsChanged" : false, "vertexSettings" : [], "allowEdgeOverflow" : false});
        }
        {
            var Q0;
            Q0=makeQuery(id+"F0.imprint","IMPRINT",FACE,{"disambiguationData":[TD([[makeQuery(id+"F0.imprint","IMPRINT",EDGE,{"derivedFrom":sQuery(id+"F0.wireOp",EDGE,"E0.top")}),-1.0]])]});
            extrude(context, id + "F16", {"entities" : qUnion([Q0]), "operationType" : NewBodyOperationType.ADD, "oppositeDirection" : true, "depth" : 15 * mm, "offsetDistance" : 25 * mm});
        }
    });
